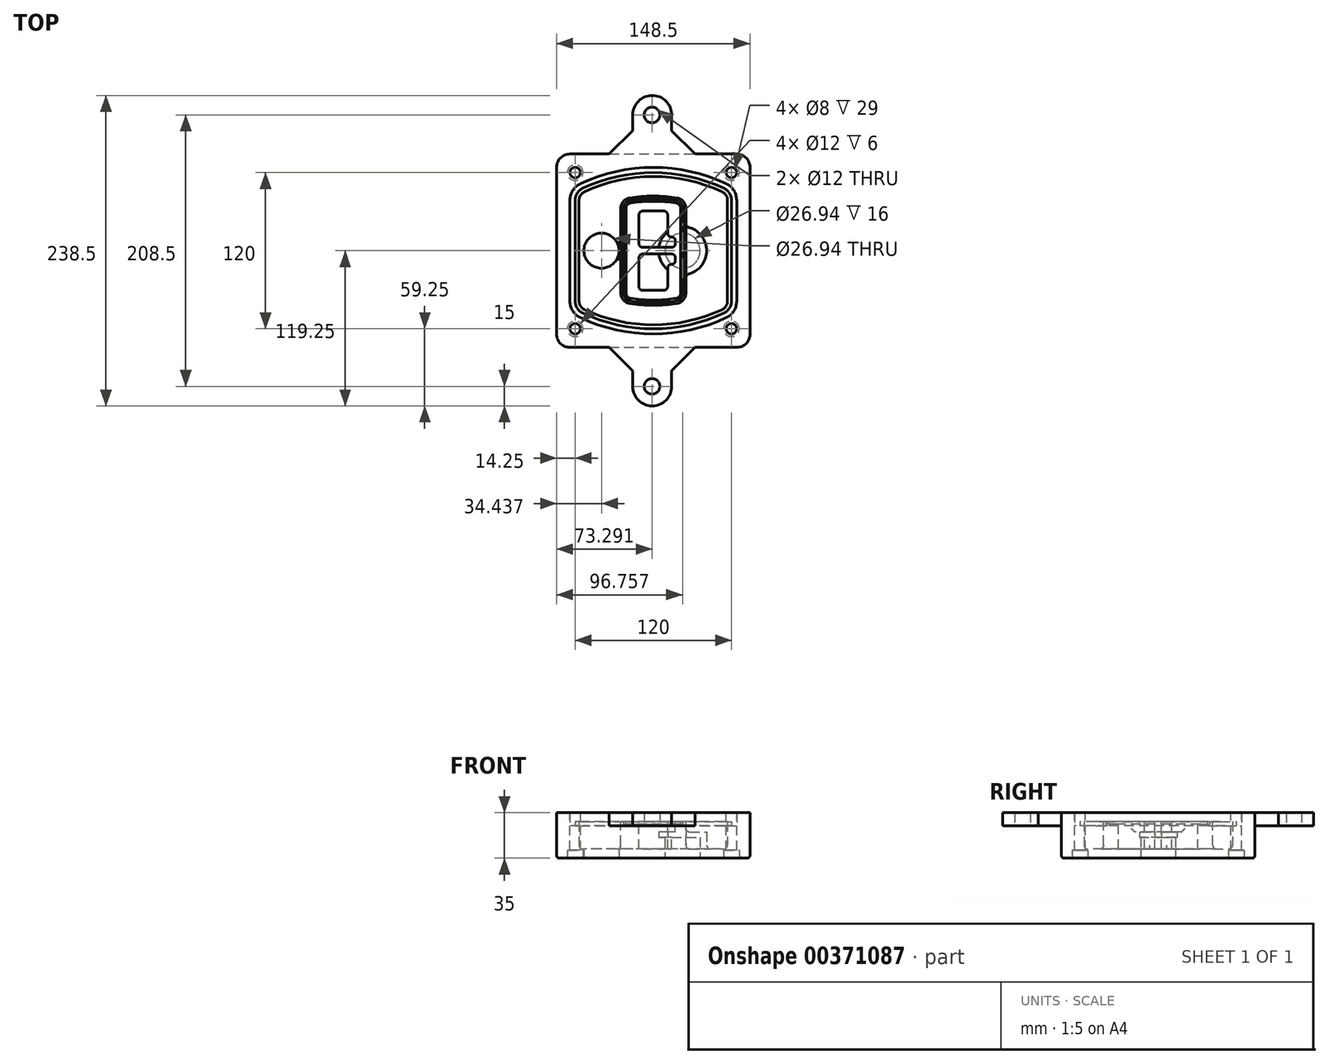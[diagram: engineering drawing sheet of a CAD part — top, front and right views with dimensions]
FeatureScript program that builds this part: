
annotation { "Feature Type Name" : "Feature", "Feature Type Description" : "" }
export const myFeature = defineFeature(function(context is Context, id is Id, definition is map)
    precondition{}
    {
        {
            var Q0;
            Q0=qCreatedBy(makeId("Top.planeOp"),FACE);
            var sketch = newSketch(context, id + "F0", { "sketchPlane" : qUnion([Q0])});
            skPoint(sketch, "E0.rect.middle", {"position": v(0, 0) * mm});
            skLineSegment(sketch, "E1.bottom", {"start": v(-64.25, -74.25) * mm, "end": v(64.25, -74.25) * mm});
            skLineSegment(sketch, "E1.top", {"start": v(-64.25, 74.25) * mm, "end": v(64.25, 74.25) * mm});
            skLineSegment(sketch, "E1.left", {"start": v(-74.25, -64.25) * mm, "end": v(-74.25, 64.25) * mm});
            skLineSegment(sketch, "E1.right", {"start": v(74.25, -64.25) * mm, "end": v(74.25, 64.25) * mm});
            skLineSegment(sketch, "E2", {"start": v(-74.25, 74.25) * mm, "end": v(74.25, -74.25) * mm, "construction": true});
            skLineSegment(sketch, "E3", {"start": v(74.25, 74.25) * mm, "end": v(-74.25, -74.25) * mm, "construction": true});
            skCircle(sketch, "E4", {"center": v(-60, 60) * mm, "radius": 4 * mm});
            skCircle(sketch, "E5", {"center": v(60, 60) * mm, "radius": 4 * mm});
            skCircle(sketch, "E6", {"center": v(60, -60) * mm, "radius": 4 * mm});
            skCircle(sketch, "E7", {"center": v(-60, -60) * mm, "radius": 4 * mm});
            skLineSegment(sketch, "E8", {"start": v(-60, 60) * mm, "end": v(60, 60) * mm, "construction": true});
            skLineSegment(sketch, "E9", {"start": v(60, 60) * mm, "end": v(60, -60) * mm, "construction": true});
            skLineSegment(sketch, "E10", {"start": v(60, -60) * mm, "end": v(-60, -60) * mm, "construction": true});
            skLineSegment(sketch, "E11", {"start": v(-60, -60) * mm, "end": v(-60, 60) * mm, "construction": true});
            skLineSegment(sketch, "E12", {"start": v(-60, 38.83) * mm, "end": v(-60, -38.83) * mm});
            skLineSegment(sketch, "E13", {"start": v(60, 38.83) * mm, "end": v(60, -38.83) * mm});
            skArc(sketch, "E14", {"start": v(54.26, 47.88) * mm, "mid": v(0, 60) * mm, "end": v(-54.26, 47.88) * mm});
            skArc(sketch, "E15", {"start": v(-54.26, -47.88) * mm, "mid": v(0, -60) * mm, "end": v(54.26, -47.88) * mm});
            skLineSegment(sketch, "E16", {"start": v(-60, 0) * mm, "end": v(60, 0) * mm, "construction": true});
            skPoint(sketch, "E17.visualSharp", {"position": v(-60, -45) * mm});
            skArc(sketch, "E17.filletArc", {"start": v(-60, -38.83) * mm, "mid": v(-58.44, -44.2) * mm, "end": v(-54.26, -47.88) * mm});
            skPoint(sketch, "E18.visualSharp", {"position": v(-60, 45) * mm});
            skArc(sketch, "E18.filletArc", {"start": v(-54.26, 47.88) * mm, "mid": v(-58.44, 44.2) * mm, "end": v(-60, 38.83) * mm});
            skPoint(sketch, "E19.visualSharp", {"position": v(60, 45) * mm});
            skArc(sketch, "E19.filletArc", {"start": v(60, 38.83) * mm, "mid": v(58.44, 44.2) * mm, "end": v(54.26, 47.88) * mm});
            skPoint(sketch, "E20.visualSharp", {"position": v(60, -45) * mm});
            skArc(sketch, "E20.filletArc", {"start": v(54.26, -47.88) * mm, "mid": v(58.44, -44.2) * mm, "end": v(60, -38.83) * mm});
            skPoint(sketch, "E21.visualSharp", {"position": v(-74.25, 74.25) * mm});
            skArc(sketch, "E21.filletArc", {"start": v(-64.25, 74.25) * mm, "mid": v(-71.32, 71.32) * mm, "end": v(-74.25, 64.25) * mm});
            skPoint(sketch, "E22.visualSharp", {"position": v(74.25, 74.25) * mm});
            skArc(sketch, "E22.filletArc", {"start": v(74.25, 64.25) * mm, "mid": v(71.32, 71.32) * mm, "end": v(64.25, 74.25) * mm});
            skPoint(sketch, "E23.visualSharp", {"position": v(74.25, -74.25) * mm});
            skArc(sketch, "E23.filletArc", {"start": v(64.25, -74.25) * mm, "mid": v(71.32, -71.32) * mm, "end": v(74.25, -64.25) * mm});
            skPoint(sketch, "E24.visualSharp", {"position": v(-74.25, -74.25) * mm});
            skArc(sketch, "E24.filletArc", {"start": v(-74.25, -64.25) * mm, "mid": v(-71.32, -71.32) * mm, "end": v(-64.25, -74.25) * mm});
            skArc(sketch, "E25.0", {"start": v(57, 38.83) * mm, "mid": v(55.9, 42.58) * mm, "end": v(52.98, 45.17) * mm});
            skLineSegment(sketch, "E25.1", {"start": v(57, 38.83) * mm, "end": v(57, -38.83) * mm});
            skArc(sketch, "E25.2", {"start": v(52.98, -45.17) * mm, "mid": v(55.9, -42.58) * mm, "end": v(57, -38.83) * mm});
            skArc(sketch, "E25.3", {"start": v(-52.98, -45.17) * mm, "mid": v(0, -57) * mm, "end": v(52.98, -45.17) * mm});
            skArc(sketch, "E25.4", {"start": v(-57, -38.83) * mm, "mid": v(-55.9, -42.58) * mm, "end": v(-52.98, -45.17) * mm});
            skArc(sketch, "E25.5", {"start": v(52.98, 45.17) * mm, "mid": v(0, 57) * mm, "end": v(-52.98, 45.17) * mm});
            skLineSegment(sketch, "E25.6", {"start": v(-57, 38.83) * mm, "end": v(-57, -38.83) * mm});
            skArc(sketch, "E25.7", {"start": v(-52.98, 45.17) * mm, "mid": v(-55.9, 42.58) * mm, "end": v(-57, 38.83) * mm});
            skArc(sketch, "E26.0", {"start": v(-55.96, 51.5) * mm, "mid": v(-61.82, 46.33) * mm, "end": v(-64, 38.83) * mm});
            skArc(sketch, "E26.1", {"start": v(55.96, 51.5) * mm, "mid": v(0, 64) * mm, "end": v(-55.96, 51.5) * mm});
            skArc(sketch, "E26.2", {"start": v(64, 38.83) * mm, "mid": v(61.82, 46.33) * mm, "end": v(55.96, 51.5) * mm});
            skLineSegment(sketch, "E26.3", {"start": v(64, 38.83) * mm, "end": v(64, -38.83) * mm});
            skArc(sketch, "E26.4", {"start": v(55.96, -51.5) * mm, "mid": v(61.82, -46.33) * mm, "end": v(64, -38.83) * mm});
            skLineSegment(sketch, "E26.5", {"start": v(-64, 38.83) * mm, "end": v(-64, -38.83) * mm});
            skArc(sketch, "E26.6", {"start": v(-55.96, -51.5) * mm, "mid": v(0, -64) * mm, "end": v(55.96, -51.5) * mm});
            skArc(sketch, "E26.7", {"start": v(-64, -38.83) * mm, "mid": v(-61.82, -46.33) * mm, "end": v(-55.96, -51.5) * mm});
            skSolve(sketch);
        }
        {
            var Q0;
            Q0=makeQuery(id+"F0.imprint","IMPRINT",FACE,{"disambiguationData":[TD([[makeQuery(id+"F0.imprint","IMPRINT",EDGE,{"derivedFrom":sQuery(id+"F0.wireOp",EDGE,"E1.bottom")}),1.0]])]});
            var Q1;
            Q1=makeQuery(id+"F0.imprint","IMPRINT",FACE,{"disambiguationData":[TD([[makeQuery(id+"F0.imprint","IMPRINT",EDGE,{"derivedFrom":sQuery(id+"F0.wireOp",EDGE,"E12")}),1.0]])]});
            var Q2;
            Q2=makeQuery(id+"F0.imprint","IMPRINT",FACE,{"disambiguationData":[TD([[makeQuery(id+"F0.imprint","IMPRINT",EDGE,{"derivedFrom":sQuery(id+"F0.wireOp",EDGE,"E25.0")}),1.0]])]});
            var Q3;
            Q3=makeQuery(id+"F0.imprint","IMPRINT",FACE,{"disambiguationData":[TD([[makeQuery(id+"F0.imprint","IMPRINT",EDGE,{"derivedFrom":sQuery(id+"F0.wireOp",EDGE,"E12")}),-1.0]])]});
            extrude(context, id + "F1", {"entities" : qUnion([Q0, Q1, Q2, Q3]), "oppositeDirection" : true, "depth" : 25 * mm});
        }
        {
            var Q0;
            Q0=makeQuery(id+"F0.imprint","IMPRINT",FACE,{"disambiguationData":[TD([[makeQuery(id+"F0.imprint","IMPRINT",EDGE,{"derivedFrom":sQuery(id+"F0.wireOp",EDGE,"E12")}),1.0]])]});
            extrude(context, id + "F2", {"entities" : qUnion([Q0]), "operationType" : NewBodyOperationType.ADD, "depth" : 3 * mm});
        }
        {
            var Q0;
            Q0=makeQuery(id+"F0.imprint","IMPRINT",FACE,{"disambiguationData":[TD([[makeQuery(id+"F0.imprint","IMPRINT",EDGE,{"derivedFrom":sQuery(id+"F0.wireOp",EDGE,"E25.0")}),1.0]])]});
            extrude(context, id + "F3", {"entities" : qUnion([Q0]), "operationType" : NewBodyOperationType.REMOVE, "oppositeDirection" : true, "depth" : 18 * mm});
        }
        {
            var Q0;
            Q0=makeQuery(id+"F2.opExtrude","CAP_FACE",FACE,{"disambiguationData":[OSD([sQuery(id+"F0.wireOp",EDGE,"E12"),sQuery(id+"F0.wireOp",EDGE,"E13"),sQuery(id+"F0.wireOp",EDGE,"E14"),sQuery(id+"F0.wireOp",EDGE,"E15"),sQuery(id+"F0.wireOp",EDGE,"E17.filletArc"),sQuery(id+"F0.wireOp",EDGE,"E18.filletArc"),sQuery(id+"F0.wireOp",EDGE,"E19.filletArc"),sQuery(id+"F0.wireOp",EDGE,"E20.filletArc"),sQuery(id+"F0.wireOp",EDGE,"E25.0"),sQuery(id+"F0.wireOp",EDGE,"E25.1"),sQuery(id+"F0.wireOp",EDGE,"E25.2"),sQuery(id+"F0.wireOp",EDGE,"E25.3"),sQuery(id+"F0.wireOp",EDGE,"E25.4"),sQuery(id+"F0.wireOp",EDGE,"E25.5"),sQuery(id+"F0.wireOp",EDGE,"E25.6"),sQuery(id+"F0.wireOp",EDGE,"E25.7")])],"isStart":false});
            var sketch = newSketch(context, id + "F4", { "sketchPlane" : qUnion([Q0])});
            skArc(sketch, "E27.0", {"start": v(-18.34, -40.45) * mm, "mid": v(0, -42) * mm, "end": v(18.34, -40.45) * mm});
            skArc(sketch, "E28.0", {"start": v(18.34, 40.45) * mm, "mid": v(0, 42) * mm, "end": v(-18.34, 40.45) * mm});
            skLineSegment(sketch, "E29", {"start": v(-25, 32.57) * mm, "end": v(-25, -32.57) * mm});
            skLineSegment(sketch, "E30", {"start": v(25, 32.57) * mm, "end": v(25, -32.57) * mm});
            skLineSegment(sketch, "E31", {"start": v(-25, 39.1) * mm, "end": v(25, 39.1) * mm, "construction": true});
            skLineSegment(sketch, "E32", {"start": v(-25, -39.1) * mm, "end": v(25, -39.1) * mm, "construction": true});
            skPoint(sketch, "E33.visualSharp", {"position": v(-25, 39.1) * mm});
            skArc(sketch, "E33.filletArc", {"start": v(-18.34, 40.45) * mm, "mid": v(-23.11, 37.73) * mm, "end": v(-25, 32.57) * mm});
            skPoint(sketch, "E34.visualSharp", {"position": v(25, 39.1) * mm});
            skArc(sketch, "E34.filletArc", {"start": v(25, 32.57) * mm, "mid": v(23.11, 37.73) * mm, "end": v(18.34, 40.45) * mm});
            skPoint(sketch, "E35.visualSharp", {"position": v(25, -39.1) * mm});
            skArc(sketch, "E35.filletArc", {"start": v(18.34, -40.45) * mm, "mid": v(23.11, -37.73) * mm, "end": v(25, -32.57) * mm});
            skPoint(sketch, "E36.visualSharp", {"position": v(-25, -39.1) * mm});
            skArc(sketch, "E36.filletArc", {"start": v(-25, -32.57) * mm, "mid": v(-23.11, -37.73) * mm, "end": v(-18.34, -40.45) * mm});
            skArc(sketch, "E37.0", {"start": v(52.98, 45.17) * mm, "mid": v(0, 57) * mm, "end": v(-52.98, 45.17) * mm});
            skArc(sketch, "E37.1", {"start": v(-52.98, 45.17) * mm, "mid": v(-55.9, 42.58) * mm, "end": v(-57, 38.83) * mm});
            skLineSegment(sketch, "E37.2", {"start": v(-57, 38.83) * mm, "end": v(-57, -38.83) * mm});
            skArc(sketch, "E37.3", {"start": v(-57, -38.83) * mm, "mid": v(-55.9, -42.58) * mm, "end": v(-52.98, -45.17) * mm});
            skArc(sketch, "E37.4", {"start": v(-52.98, -45.17) * mm, "mid": v(0, -57) * mm, "end": v(52.98, -45.17) * mm});
            skArc(sketch, "E37.5", {"start": v(52.98, -45.17) * mm, "mid": v(55.9, -42.58) * mm, "end": v(57, -38.83) * mm});
            skLineSegment(sketch, "E37.6", {"start": v(57, 38.83) * mm, "end": v(57, -38.83) * mm});
            skArc(sketch, "E37.7", {"start": v(57, 38.83) * mm, "mid": v(55.9, 42.58) * mm, "end": v(52.98, 45.17) * mm});
            skLineSegment(sketch, "E38.0", {"start": v(23, 32.57) * mm, "end": v(23, -32.57) * mm});
            skArc(sketch, "E38.1", {"start": v(18, -38.48) * mm, "mid": v(21.58, -36.44) * mm, "end": v(23, -32.57) * mm});
            skArc(sketch, "E38.2", {"start": v(-18, -38.48) * mm, "mid": v(0, -40) * mm, "end": v(18, -38.48) * mm});
            skArc(sketch, "E38.3", {"start": v(-23, -32.57) * mm, "mid": v(-21.58, -36.44) * mm, "end": v(-18, -38.48) * mm});
            skLineSegment(sketch, "E38.4", {"start": v(-23, 32.57) * mm, "end": v(-23, -32.57) * mm});
            skArc(sketch, "E38.5", {"start": v(23, 32.57) * mm, "mid": v(21.58, 36.44) * mm, "end": v(18, 38.48) * mm});
            skArc(sketch, "E38.6", {"start": v(-18, 38.48) * mm, "mid": v(-21.58, 36.44) * mm, "end": v(-23, 32.57) * mm});
            skArc(sketch, "E38.7", {"start": v(18, 38.48) * mm, "mid": v(0, 40) * mm, "end": v(-18, 38.48) * mm});
            skArc(sketch, "E39.0", {"start": v(21, 32.57) * mm, "mid": v(20.06, 35.15) * mm, "end": v(17.67, 36.5) * mm});
            skLineSegment(sketch, "E39.1", {"start": v(21, 32.57) * mm, "end": v(21, -32.57) * mm});
            skArc(sketch, "E39.2", {"start": v(17.67, -36.5) * mm, "mid": v(20.06, -35.15) * mm, "end": v(21, -32.57) * mm});
            skArc(sketch, "E39.3", {"start": v(-17.67, -36.5) * mm, "mid": v(0, -38) * mm, "end": v(17.67, -36.5) * mm});
            skArc(sketch, "E39.4", {"start": v(-21, -32.57) * mm, "mid": v(-20.06, -35.15) * mm, "end": v(-17.67, -36.5) * mm});
            skArc(sketch, "E39.5", {"start": v(17.67, 36.5) * mm, "mid": v(0, 38) * mm, "end": v(-17.67, 36.5) * mm});
            skLineSegment(sketch, "E39.6", {"start": v(-21, 32.57) * mm, "end": v(-21, -32.57) * mm});
            skArc(sketch, "E39.7", {"start": v(-17.67, 36.5) * mm, "mid": v(-20.06, 35.15) * mm, "end": v(-21, 32.57) * mm});
            skLineSegment(sketch, "E40", {"start": v(-25, 0) * mm, "end": v(25, 0) * mm, "construction": true});
            skLineSegment(sketch, "E41", {"start": v(-11, 5.5) * mm, "end": v(-11, 27.5) * mm});
            skLineSegment(sketch, "E42", {"start": v(-8, 30.5) * mm, "end": v(8, 30.5) * mm});
            skLineSegment(sketch, "E43", {"start": v(11, 27.5) * mm, "end": v(11, 13.5) * mm});
            skLineSegment(sketch, "E44", {"start": v(14, 10.5) * mm, "end": v(14, 10.5) * mm});
            skLineSegment(sketch, "E45", {"start": v(17, 7.5) * mm, "end": v(17, 5.5) * mm});
            skLineSegment(sketch, "E46", {"start": v(14, 2.5) * mm, "end": v(-8, 2.5) * mm});
            skPoint(sketch, "E47.visualSharp", {"position": v(-11, 30.5) * mm});
            skArc(sketch, "E47.filletArc", {"start": v(-8, 30.5) * mm, "mid": v(-10.12, 29.62) * mm, "end": v(-11, 27.5) * mm});
            skPoint(sketch, "E48.visualSharp", {"position": v(11, 30.5) * mm});
            skArc(sketch, "E48.filletArc", {"start": v(11, 27.5) * mm, "mid": v(10.12, 29.62) * mm, "end": v(8, 30.5) * mm});
            skPoint(sketch, "E49.visualSharp", {"position": v(11, 10.5) * mm});
            skArc(sketch, "E49.filletArc", {"start": v(11, 13.5) * mm, "mid": v(11.88, 11.38) * mm, "end": v(14, 10.5) * mm});
            skPoint(sketch, "E50.visualSharp", {"position": v(17, 10.5) * mm});
            skArc(sketch, "E50.filletArc", {"start": v(17, 7.5) * mm, "mid": v(16.12, 9.62) * mm, "end": v(14, 10.5) * mm});
            skPoint(sketch, "E51.visualSharp", {"position": v(17, 2.5) * mm});
            skArc(sketch, "E51.filletArc", {"start": v(14, 2.5) * mm, "mid": v(16.12, 3.38) * mm, "end": v(17, 5.5) * mm});
            skPoint(sketch, "E52.visualSharp", {"position": v(-11, 2.5) * mm});
            skArc(sketch, "E52.filletArc", {"start": v(-11, 5.5) * mm, "mid": v(-10.12, 3.38) * mm, "end": v(-8, 2.5) * mm});
            skLineSegment(sketch, "E53.0.MirrorCS", {"start": v(14, -2.5) * mm, "end": v(-8, -2.5) * mm});
            skArc(sketch, "E54.0.MirrorCS", {"start": v(-11, -5.5) * mm, "mid": v(-10.12, -3.38) * mm, "end": v(-8, -2.5) * mm});
            skLineSegment(sketch, "E55.0.MirrorCS", {"start": v(-11, -5.5) * mm, "end": v(-11, -27.5) * mm});
            skArc(sketch, "E56.0.MirrorCS", {"start": v(-8, -30.5) * mm, "mid": v(-10.12, -29.62) * mm, "end": v(-11, -27.5) * mm});
            skLineSegment(sketch, "E57.0.MirrorCS", {"start": v(-8, -30.5) * mm, "end": v(8, -30.5) * mm});
            skArc(sketch, "E58.0.MirrorCS", {"start": v(11, -27.5) * mm, "mid": v(10.12, -29.62) * mm, "end": v(8, -30.5) * mm});
            skLineSegment(sketch, "E59.0.MirrorCS", {"start": v(11, -27.5) * mm, "end": v(11, -13.5) * mm});
            skArc(sketch, "E60.0.MirrorCS", {"start": v(11, -13.5) * mm, "mid": v(11.88, -11.38) * mm, "end": v(14, -10.5) * mm});
            skArc(sketch, "E61.0.MirrorCS", {"start": v(17, -7.5) * mm, "mid": v(16.12, -9.62) * mm, "end": v(14, -10.5) * mm});
            skLineSegment(sketch, "E62.0.MirrorCS", {"start": v(17, -7.5) * mm, "end": v(17, -5.5) * mm});
            skArc(sketch, "E63.0.MirrorCS", {"start": v(14, -2.5) * mm, "mid": v(16.12, -3.38) * mm, "end": v(17, -5.5) * mm});
            skSolve(sketch);
        }
        {
            var Q0;
            Q0=makeQuery(id+"F4.imprint","IMPRINT",FACE,{"disambiguationData":[TD([[makeQuery(id+"F4.imprint","IMPRINT",EDGE,{"derivedFrom":sQuery(id+"F4.wireOp",EDGE,"E27.0")}),1.0]])]});
            var Q1;
            Q1=makeQuery(id+"F4.imprint","IMPRINT",FACE,{"disambiguationData":[TD([[makeQuery(id+"F4.imprint","IMPRINT",EDGE,{"derivedFrom":sQuery(id+"F4.wireOp",EDGE,"E38.0")}),-1.0]])]});
            var Q2;
            Q2=makeQuery(id+"F4.imprint","IMPRINT",FACE,{"disambiguationData":[TD([[makeQuery(id+"F4.imprint","IMPRINT",EDGE,{"derivedFrom":sQuery(id+"F4.wireOp",EDGE,"E39.0")}),1.0]])]});
            extrude(context, id + "F5", {"entities" : qUnion([Q0, Q1, Q2]), "operationType" : NewBodyOperationType.ADD, "endBound" : BoundingType.UP_TO_NEXT, "oppositeDirection" : true, "depth" : 25 * mm});
        }
        {
            var Q0;
            Q0=makeQuery(id+"F4.imprint","IMPRINT",FACE,{"disambiguationData":[TD([[makeQuery(id+"F4.imprint","IMPRINT",EDGE,{"derivedFrom":sQuery(id+"F4.wireOp",EDGE,"E38.0")}),-1.0]])]});
            extrude(context, id + "F6", {"entities" : qUnion([Q0]), "operationType" : NewBodyOperationType.REMOVE, "oppositeDirection" : true, "depth" : 2 * mm});
        }
        {
            var Q0;
            Q0=makeQuery(id+"F1.opExtrude","CAP_FACE",FACE,{"disambiguationData":[OSD([sQuery(id+"F0.wireOp",EDGE,"E1.bottom"),sQuery(id+"F0.wireOp",EDGE,"E1.top"),sQuery(id+"F0.wireOp",EDGE,"E1.left"),sQuery(id+"F0.wireOp",EDGE,"E1.right"),sQuery(id+"F0.wireOp",EDGE,"E4"),sQuery(id+"F0.wireOp",EDGE,"E5"),sQuery(id+"F0.wireOp",EDGE,"E6"),sQuery(id+"F0.wireOp",EDGE,"E7"),sQuery(id+"F0.wireOp",EDGE,"E21.filletArc"),sQuery(id+"F0.wireOp",EDGE,"E22.filletArc"),sQuery(id+"F0.wireOp",EDGE,"E23.filletArc"),sQuery(id+"F0.wireOp",EDGE,"E24.filletArc")])],"isStart":false});
            var sketch = newSketch(context, id + "F7", { "sketchPlane" : qUnion([Q0])});
            skCircle(sketch, "E64", {"center": v(22.5, 0) * mm, "radius": 13.47 * mm});
            skCircle(sketch, "E65", {"center": v(-39.81, 0) * mm, "radius": 13.47 * mm});
            skLineSegment(sketch, "E66", {"start": v(74.25, 0) * mm, "end": v(-74.25, 0) * mm});
            skCircle(sketch, "E67", {"center": v(22.5, 0) * mm, "radius": 18.47 * mm});
            skCircle(sketch, "E68", {"center": v(60, -60) * mm, "radius": 6 * mm});
            skCircle(sketch, "E69", {"center": v(-60, -60) * mm, "radius": 6 * mm});
            skCircle(sketch, "E70", {"center": v(-60, 60) * mm, "radius": 6 * mm});
            skCircle(sketch, "E71", {"center": v(60, 60) * mm, "radius": 6 * mm});
            skSolve(sketch);
        }
        {
            var Q0;
            {var subQ1=sQuery(id+"F7.wireOp",EDGE,"E66");var subQ4=sQuery(id+"F7.wireOp",EDGE,"E64");var subQ6=makeQuery(id+"F7.imprint","INTERSECT",VERTEX,{"disambiguationData":[OD(0.0)],"derivedFrom":[subQ4,subQ1]});Q0=makeQuery(id+"F7.imprint","IMPRINT",FACE,{"disambiguationData":[TD([[makeQuery(id+"F7.imprint","IMPRINT",EDGE,{"disambiguationData":[TD([[subQ6,-1.0]])],"derivedFrom":subQ4}),-1.0]])]});}
            var Q1;
            {var subQ0=sQuery(id+"F7.wireOp",EDGE,"E66");var subQ1=sQuery(id+"F7.wireOp",EDGE,"E64");var subQ3=makeQuery(id+"F7.imprint","INTERSECT",VERTEX,{"disambiguationData":[OD(0.0)],"derivedFrom":[subQ1,subQ0]});Q1=makeQuery(id+"F7.imprint","IMPRINT",FACE,{"disambiguationData":[TD([[makeQuery(id+"F7.imprint","IMPRINT",EDGE,{"disambiguationData":[TD([[subQ3,-1.0]])],"derivedFrom":subQ1}),1.0]])]});}
            var Q2;
            {var subQ0=sQuery(id+"F7.wireOp",EDGE,"E66");var subQ1=sQuery(id+"F7.wireOp",EDGE,"E64");var subQ3=makeQuery(id+"F7.imprint","INTERSECT",VERTEX,{"disambiguationData":[OD(0.0)],"derivedFrom":[subQ1,subQ0]});Q2=makeQuery(id+"F7.imprint","IMPRINT",FACE,{"disambiguationData":[TD([[makeQuery(id+"F7.imprint","IMPRINT",EDGE,{"disambiguationData":[TD([[subQ3,1.0]])],"derivedFrom":subQ1}),1.0]])]});}
            var Q3;
            {var subQ1=sQuery(id+"F7.wireOp",EDGE,"E66");var subQ4=sQuery(id+"F7.wireOp",EDGE,"E64");var subQ6=makeQuery(id+"F7.imprint","INTERSECT",VERTEX,{"disambiguationData":[OD(0.0)],"derivedFrom":[subQ4,subQ1]});Q3=makeQuery(id+"F7.imprint","IMPRINT",FACE,{"disambiguationData":[TD([[makeQuery(id+"F7.imprint","IMPRINT",EDGE,{"disambiguationData":[TD([[subQ6,1.0]])],"derivedFrom":subQ4}),-1.0]])]});}
            extrude(context, id + "F8", {"entities" : qUnion([Q0, Q1, Q2, Q3]), "operationType" : NewBodyOperationType.ADD, "oppositeDirection" : true, "depth" : 20 * mm});
        }
        {
            var Q0;
            {var subQ0=sQuery(id+"F7.wireOp",EDGE,"E66");var subQ1=sQuery(id+"F7.wireOp",EDGE,"E64");var subQ3=makeQuery(id+"F7.imprint","INTERSECT",VERTEX,{"disambiguationData":[OD(0.0)],"derivedFrom":[subQ1,subQ0]});Q0=makeQuery(id+"F7.imprint","IMPRINT",FACE,{"disambiguationData":[TD([[makeQuery(id+"F7.imprint","IMPRINT",EDGE,{"disambiguationData":[TD([[subQ3,-1.0]])],"derivedFrom":subQ1}),1.0]])]});}
            var Q1;
            {var subQ0=sQuery(id+"F7.wireOp",EDGE,"E66");var subQ1=sQuery(id+"F7.wireOp",EDGE,"E64");var subQ3=makeQuery(id+"F7.imprint","INTERSECT",VERTEX,{"disambiguationData":[OD(0.0)],"derivedFrom":[subQ1,subQ0]});Q1=makeQuery(id+"F7.imprint","IMPRINT",FACE,{"disambiguationData":[TD([[makeQuery(id+"F7.imprint","IMPRINT",EDGE,{"disambiguationData":[TD([[subQ3,1.0]])],"derivedFrom":subQ1}),1.0]])]});}
            extrude(context, id + "F9", {"entities" : qUnion([Q0, Q1]), "operationType" : NewBodyOperationType.REMOVE, "oppositeDirection" : true, "depth" : 16 * mm});
        }
        {
            var Q0;
            {var subQ0=sQuery(id+"F7.wireOp",EDGE,"E66");var subQ1=sQuery(id+"F7.wireOp",EDGE,"E65");var subQ3=makeQuery(id+"F7.imprint","INTERSECT",VERTEX,{"disambiguationData":[OD(0.0)],"derivedFrom":[subQ1,subQ0]});Q0=makeQuery(id+"F7.imprint","IMPRINT",FACE,{"disambiguationData":[TD([[makeQuery(id+"F7.imprint","IMPRINT",EDGE,{"disambiguationData":[TD([[subQ3,-1.0]])],"derivedFrom":subQ1}),1.0]])]});}
            var Q1;
            {var subQ0=sQuery(id+"F7.wireOp",EDGE,"E66");var subQ1=sQuery(id+"F7.wireOp",EDGE,"E65");var subQ3=makeQuery(id+"F7.imprint","INTERSECT",VERTEX,{"disambiguationData":[OD(0.0)],"derivedFrom":[subQ1,subQ0]});Q1=makeQuery(id+"F7.imprint","IMPRINT",FACE,{"disambiguationData":[TD([[makeQuery(id+"F7.imprint","IMPRINT",EDGE,{"disambiguationData":[TD([[subQ3,1.0]])],"derivedFrom":subQ1}),1.0]])]});}
            extrude(context, id + "F10", {"entities" : qUnion([Q0, Q1]), "operationType" : NewBodyOperationType.REMOVE, "oppositeDirection" : true, "depth" : 25 * mm});
        }
        {
            var Q0;
            Q0=makeQuery(id+"F7.imprint","IMPRINT",FACE,{"disambiguationData":[TD([[makeQuery(id+"F7.imprint","IMPRINT",EDGE,{"derivedFrom":sQuery(id+"F7.wireOp",EDGE,"E68")}),1.0]])]});
            var Q1;
            Q1=makeQuery(id+"F7.imprint","IMPRINT",FACE,{"disambiguationData":[TD([[makeQuery(id+"F7.imprint","IMPRINT",EDGE,{"derivedFrom":makeQuery(id+"F1.opExtrude","CAP_EDGE",EDGE,{"disambiguationData":[OSD([sQuery(id+"F0.wireOp",EDGE,"E5")])],"isStart":false})}),-1.0]])]});
            var Q2;
            Q2=makeQuery(id+"F7.imprint","IMPRINT",FACE,{"disambiguationData":[TD([[makeQuery(id+"F7.imprint","IMPRINT",EDGE,{"derivedFrom":sQuery(id+"F7.wireOp",EDGE,"E69")}),1.0]])]});
            var Q3;
            Q3=makeQuery(id+"F7.imprint","IMPRINT",FACE,{"disambiguationData":[TD([[makeQuery(id+"F7.imprint","IMPRINT",EDGE,{"derivedFrom":makeQuery(id+"F1.opExtrude","CAP_EDGE",EDGE,{"disambiguationData":[OSD([sQuery(id+"F0.wireOp",EDGE,"E4")])],"isStart":false})}),-1.0]])]});
            var Q4;
            Q4=makeQuery(id+"F7.imprint","IMPRINT",FACE,{"disambiguationData":[TD([[makeQuery(id+"F7.imprint","IMPRINT",EDGE,{"derivedFrom":sQuery(id+"F7.wireOp",EDGE,"E70")}),1.0]])]});
            var Q5;
            Q5=makeQuery(id+"F7.imprint","IMPRINT",FACE,{"disambiguationData":[TD([[makeQuery(id+"F7.imprint","IMPRINT",EDGE,{"derivedFrom":makeQuery(id+"F1.opExtrude","CAP_EDGE",EDGE,{"disambiguationData":[OSD([sQuery(id+"F0.wireOp",EDGE,"E7")])],"isStart":false})}),-1.0]])]});
            var Q6;
            Q6=makeQuery(id+"F7.imprint","IMPRINT",FACE,{"disambiguationData":[TD([[makeQuery(id+"F7.imprint","IMPRINT",EDGE,{"derivedFrom":sQuery(id+"F7.wireOp",EDGE,"E71")}),1.0]])]});
            var Q7;
            Q7=makeQuery(id+"F7.imprint","IMPRINT",FACE,{"disambiguationData":[TD([[makeQuery(id+"F7.imprint","IMPRINT",EDGE,{"derivedFrom":makeQuery(id+"F1.opExtrude","CAP_EDGE",EDGE,{"disambiguationData":[OSD([sQuery(id+"F0.wireOp",EDGE,"E6")])],"isStart":false})}),-1.0]])]});
            extrude(context, id + "F11", {"entities" : qUnion([Q0, Q1, Q2, Q3, Q4, Q5, Q6, Q7]), "operationType" : NewBodyOperationType.REMOVE, "oppositeDirection" : true, "depth" : 6 * mm});
        }
        {
            var Q0;
            Q0=makeQuery(id+"F9.boolean.opBoolean","COPY",FACE,{"derivedFrom":makeQuery(id+"F9.opExtrude","CAP_FACE",FACE,{"disambiguationData":[OSD([sQuery(id+"F7.wireOp",EDGE,"E64")])],"isStart":false})});
            var sketch = newSketch(context, id + "F12", { "sketchPlane" : qUnion([Q0])});
            skArc(sketch, "E72.0", {"start": v(11, 14.45) * mm, "mid": v(6.45, 9.13) * mm, "end": v(4.2, 2.5) * mm});
            skArc(sketch, "E72.1", {"start": v(4.2, -2.5) * mm, "mid": v(6.45, -9.13) * mm, "end": v(11, -14.45) * mm});
            skLineSegment(sketch, "E73", {"start": v(4.2, -2.5) * mm, "end": v(14, -2.5) * mm});
            skLineSegment(sketch, "E74.0", {"start": v(14, 2.5) * mm, "end": v(4.2, 2.5) * mm});
            skArc(sketch, "E74.1", {"start": v(14, 2.5) * mm, "mid": v(16.12, 3.38) * mm, "end": v(17, 5.5) * mm});
            skLineSegment(sketch, "E74.2", {"start": v(17, 7.5) * mm, "end": v(17, 5.5) * mm});
            skArc(sketch, "E74.3", {"start": v(17, 7.5) * mm, "mid": v(16.12, 9.62) * mm, "end": v(14, 10.5) * mm});
            skArc(sketch, "E74.4", {"start": v(11, 13.5) * mm, "mid": v(11.88, 11.38) * mm, "end": v(14, 10.5) * mm});
            skLineSegment(sketch, "E74.5", {"start": v(11, 14.45) * mm, "end": v(11, 13.5) * mm});
            skLineSegment(sketch, "E74.7", {"start": v(14, -2.5) * mm, "end": v(4.2, -2.5) * mm});
            skArc(sketch, "E74.8", {"start": v(14, -2.5) * mm, "mid": v(16.12, -3.38) * mm, "end": v(17, -5.5) * mm});
            skLineSegment(sketch, "E74.9", {"start": v(17, -7.5) * mm, "end": v(17, -5.5) * mm});
            skArc(sketch, "E74.10", {"start": v(17, -7.5) * mm, "mid": v(16.12, -9.62) * mm, "end": v(14, -10.5) * mm});
            skArc(sketch, "E74.11", {"start": v(11, -13.5) * mm, "mid": v(11.88, -11.38) * mm, "end": v(14, -10.5) * mm});
            skLineSegment(sketch, "E74.12", {"start": v(11, -14.45) * mm, "end": v(11, -13.5) * mm});
            skPoint(sketch, "E75.orphan", {"position": v(11, -27.5) * mm});
            skPoint(sketch, "E76.orphan", {"position": v(-8, -2.5) * mm});
            skPoint(sketch, "E77.orphan", {"position": v(-8, 2.5) * mm});
            skPoint(sketch, "E78.orphan", {"position": v(11, 27.5) * mm});
            skSolve(sketch);
        }
        {
            var Q0;
            {var subQ7=sQuery(id+"F12.wireOp",EDGE,"E72.0");var subQ14=sQuery(id+"F12.wireOp",EDGE,"E72.1");var subQ16=sQuery(id+"F12.wireOp",EDGE,"E74.1");var subQ18=sQuery(id+"F12.wireOp",EDGE,"E74.8");Q0=qUnion([makeQuery(id+"F12.imprint","IMPRINT",FACE,{"disambiguationData":[TD([[makeQuery(id+"F12.imprint","IMPRINT",EDGE,{"derivedFrom":subQ7}),1.0]])]}),makeQuery(id+"F12.imprint","IMPRINT",FACE,{"disambiguationData":[TD([[makeQuery(id+"F12.imprint","IMPRINT",EDGE,{"derivedFrom":subQ14}),1.0]])]}),makeQuery(id+"F12.imprint","IMPRINT",FACE,{"disambiguationData":[TD([[makeQuery(id+"F12.imprint","IMPRINT",EDGE,{"derivedFrom":subQ16}),1.0]])]}),makeQuery(id+"F12.imprint","IMPRINT",FACE,{"disambiguationData":[TD([[makeQuery(id+"F12.imprint","IMPRINT",EDGE,{"derivedFrom":subQ18}),-1.0]])]})]);}
            var Q1;
            Q1=makeQuery(id+"F5.boolean.opBoolean","SPLIT",FACE,{"disambiguationData":[TD([makeQuery(id+"F5.opExtrude","SWEPT_FACE",FACE,{"disambiguationData":[OSD([sQuery(id+"F4.wireOp",EDGE,"E41")])]})])],"derivedFrom":makeQuery(id+"F3.boolean.opBoolean","COPY",FACE,{"derivedFrom":makeQuery(id+"F3.opExtrude","CAP_FACE",FACE,{"disambiguationData":[OSD([sQuery(id+"F0.wireOp",EDGE,"E25.0"),sQuery(id+"F0.wireOp",EDGE,"E25.1"),sQuery(id+"F0.wireOp",EDGE,"E25.2"),sQuery(id+"F0.wireOp",EDGE,"E25.3"),sQuery(id+"F0.wireOp",EDGE,"E25.4"),sQuery(id+"F0.wireOp",EDGE,"E25.5"),sQuery(id+"F0.wireOp",EDGE,"E25.6"),sQuery(id+"F0.wireOp",EDGE,"E25.7")])],"isStart":false})})});
            extrude(context, id + "F13", {"entities" : qUnion([Q0]), "operationType" : NewBodyOperationType.REMOVE, "endBound" : BoundingType.UP_TO_SURFACE, "endBoundEntityFace" : qUnion([Q1]), "depth" : 25 * mm});
        }
        {
            var Q0;
            Q0=makeQuery(id+"F3.boolean.opBoolean","COPY",EDGE,{"derivedFrom":makeQuery(id+"F3.opExtrude","CAP_EDGE",EDGE,{"disambiguationData":[OSD([sQuery(id+"F0.wireOp",EDGE,"E25.6")])],"isStart":false})});
            var Q1;
            Q1=makeQuery(id+"F8.boolean.opBoolean","INTERSECT",EDGE,{"derivedFrom":[makeQuery(id+"F5.opExtrude","SWEPT_FACE",FACE,{"disambiguationData":[OSD([sQuery(id+"F4.wireOp",EDGE,"E30")])]}),makeQuery(id+"F8.opExtrude","CAP_FACE",FACE,{"disambiguationData":[OSD([sQuery(id+"F7.wireOp",EDGE,"E67")])],"isStart":false})]});
            var Q2;
            Q2=makeQuery(id+"F8.boolean.opBoolean","INTERSECT",EDGE,{"disambiguationData":[OD(1.0)],"derivedFrom":[makeQuery(id+"F5.opExtrude","SWEPT_FACE",FACE,{"disambiguationData":[OSD([sQuery(id+"F4.wireOp",EDGE,"E30")])]}),makeQuery(id+"F8.opExtrude","SWEPT_FACE",FACE,{"disambiguationData":[OSD([sQuery(id+"F7.wireOp",EDGE,"E67")])]})]});
            var Q3;
            {var subQ0=sQuery(id+"F4.wireOp",EDGE,"E30");Q3=makeQuery(id+"F8.boolean.opBoolean","SPLIT",EDGE,{"disambiguationData":[TD([makeQuery(id+"F5.opExtrude","SWEPT_FACE",FACE,{"disambiguationData":[OSD([sQuery(id+"F4.wireOp",EDGE,"E35.filletArc")])]})])],"derivedFrom":makeQuery(id+"F5.opExtrude","CAP_EDGE",EDGE,{"disambiguationData":[OSD([subQ0])],"isStart":false})});}
            var Q4;
            {var subQ0=sQuery(id+"F0.wireOp",EDGE,"E25.7");var subQ1=sQuery(id+"F0.wireOp",EDGE,"E25.1");var subQ2=sQuery(id+"F0.wireOp",EDGE,"E25.6");var subQ3=sQuery(id+"F0.wireOp",EDGE,"E25.5");var subQ4=sQuery(id+"F0.wireOp",EDGE,"E25.4");var subQ5=sQuery(id+"F0.wireOp",EDGE,"E25.0");var subQ6=sQuery(id+"F0.wireOp",EDGE,"E25.2");var subQ7=sQuery(id+"F0.wireOp",EDGE,"E25.3");Q4=makeQuery(id+"F8.boolean.opBoolean","INTERSECT",EDGE,{"derivedFrom":[makeQuery(id+"F5.boolean.opBoolean","SPLIT",FACE,{"disambiguationData":[TD([makeQuery(id+"F2.opExtrude","SWEPT_FACE",FACE,{"disambiguationData":[OSD([subQ5])]})])],"derivedFrom":makeQuery(id+"F3.boolean.opBoolean","COPY",FACE,{"derivedFrom":makeQuery(id+"F3.opExtrude","CAP_FACE",FACE,{"disambiguationData":[OSD([subQ5,subQ1,subQ6,subQ7,subQ4,subQ3,subQ2,subQ0])],"isStart":false})})}),makeQuery(id+"F8.opExtrude","SWEPT_FACE",FACE,{"disambiguationData":[OSD([sQuery(id+"F7.wireOp",EDGE,"E67")])]})]});}
            var Q5;
            Q5=makeQuery(id+"F8.boolean.opBoolean","INTERSECT",EDGE,{"disambiguationData":[OD(0.0)],"derivedFrom":[makeQuery(id+"F5.opExtrude","SWEPT_FACE",FACE,{"disambiguationData":[OSD([sQuery(id+"F4.wireOp",EDGE,"E30")])]}),makeQuery(id+"F8.opExtrude","SWEPT_FACE",FACE,{"disambiguationData":[OSD([sQuery(id+"F7.wireOp",EDGE,"E67")])]})]});
            fillet(context, id + "F14", {"entities" : qUnion([Q0, Q1, Q2, Q3, Q4, Q5]), "radius" : 3 * mm, "tangentPropagation" : true, "allowEdgeOverflow" : false});
        }
        {
            var Q0;
            Q0=makeQuery(id+"F1.opExtrude","CAP_EDGE",EDGE,{"disambiguationData":[OSD([sQuery(id+"F0.wireOp",EDGE,"E1.bottom")])],"isStart":false});
            fillet(context, id + "F15", {"entities" : qUnion([Q0]), "radius" : 2 * mm, "tangentPropagation" : true, "allowEdgeOverflow" : false});
        }
        {
            var Q0;
            Q0=makeQuery(id+"F0.imprint","IMPRINT",FACE,{"disambiguationData":[TD([[makeQuery(id+"F0.imprint","IMPRINT",EDGE,{"derivedFrom":sQuery(id+"F0.wireOp",EDGE,"E1.bottom")}),1.0]])]});
            var sketch = newSketch(context, id + "F16", { "sketchPlane" : qUnion([Q0])});
            skCircle(sketch, "E79", {"center": v(-0.96, 104.25) * mm, "radius": 6 * mm});
            skLineSegment(sketch, "E80", {"start": v(-0.88, 104.89) * mm, "end": v(-0.88, 74.89) * mm, "construction": true});
            skLineSegment(sketch, "E81", {"start": v(-15.88, 104.25) * mm, "end": v(-15.88, 92.25) * mm});
            skLineSegment(sketch, "E82", {"start": v(-15.88, 92.25) * mm, "end": v(-34.5, 73.64) * mm});
            skLineSegment(sketch, "E83.MirrorCS", {"start": v(14.12, 104.25) * mm, "end": v(14.12, 92.25) * mm});
            skLineSegment(sketch, "E84.MirrorCS", {"start": v(14.12, 92.25) * mm, "end": v(32.72, 73.64) * mm});
            skArc(sketch, "E85", {"start": v(14.12, 104.25) * mm, "mid": v(-0.88, 119.25) * mm, "end": v(-15.88, 104.25) * mm});
            skLineSegment(sketch, "E86", {"start": v(-74.98, 0) * mm, "end": v(74.35, 0) * mm, "construction": true});
            skLineSegment(sketch, "E87.MirrorCS", {"start": v(-15.88, -92.25) * mm, "end": v(-34.5, -73.64) * mm});
            skLineSegment(sketch, "E88.MirrorCS", {"start": v(-15.88, -104.25) * mm, "end": v(-15.88, -92.25) * mm});
            skArc(sketch, "E89.MirrorCS", {"start": v(14.12, -104.25) * mm, "mid": v(-0.88, -119.25) * mm, "end": v(-15.88, -104.25) * mm});
            skCircle(sketch, "E90.MirrorC", {"center": v(-0.96, -104.25) * mm, "radius": 6 * mm});
            skLineSegment(sketch, "E91.MirrorCS", {"start": v(-0.88, -104.89) * mm, "end": v(-0.88, -74.89) * mm, "construction": true});
            skLineSegment(sketch, "E92.MirrorCS", {"start": v(14.12, -104.25) * mm, "end": v(14.12, -92.25) * mm});
            skLineSegment(sketch, "E93.MirrorCS", {"start": v(14.12, -92.25) * mm, "end": v(32.72, -73.64) * mm});
            skSolve(sketch);
        }
        {
            var Q0;
            Q0=makeQuery(id+"F16.imprint","IMPRINT",FACE,{"disambiguationData":[TD([[makeQuery(id+"F16.imprint","IMPRINT",EDGE,{"derivedFrom":sQuery(id+"F16.wireOp",EDGE,"E79")}),-1.0]])]});
            var Q1;
            {var subQ0=sQuery(id+"F16.wireOp",EDGE,"E88.MirrorCS");Q1=makeQuery(id+"F16.imprint","IMPRINT",FACE,{"disambiguationData":[TD([[makeQuery(id+"F16.imprint","IMPRINT",EDGE,{"derivedFrom":subQ0}),-1.0]])]});}
            var Q2;
            Q2=makeQuery(id+"F16.imprint","IMPRINT",FACE,{"disambiguationData":[TD([[makeQuery(id+"F16.imprint","IMPRINT",EDGE,{"derivedFrom":makeQuery(id+"F0.imprint","IMPRINT",EDGE,{"derivedFrom":sQuery(id+"F0.wireOp",EDGE,"E1.left")})}),-1.0]])]});
            extrude(context, id + "F17", {"entities" : qUnion([Q0, Q1, Q2]), "operationType" : NewBodyOperationType.ADD, "depth" : 10 * mm});
        }
    });
